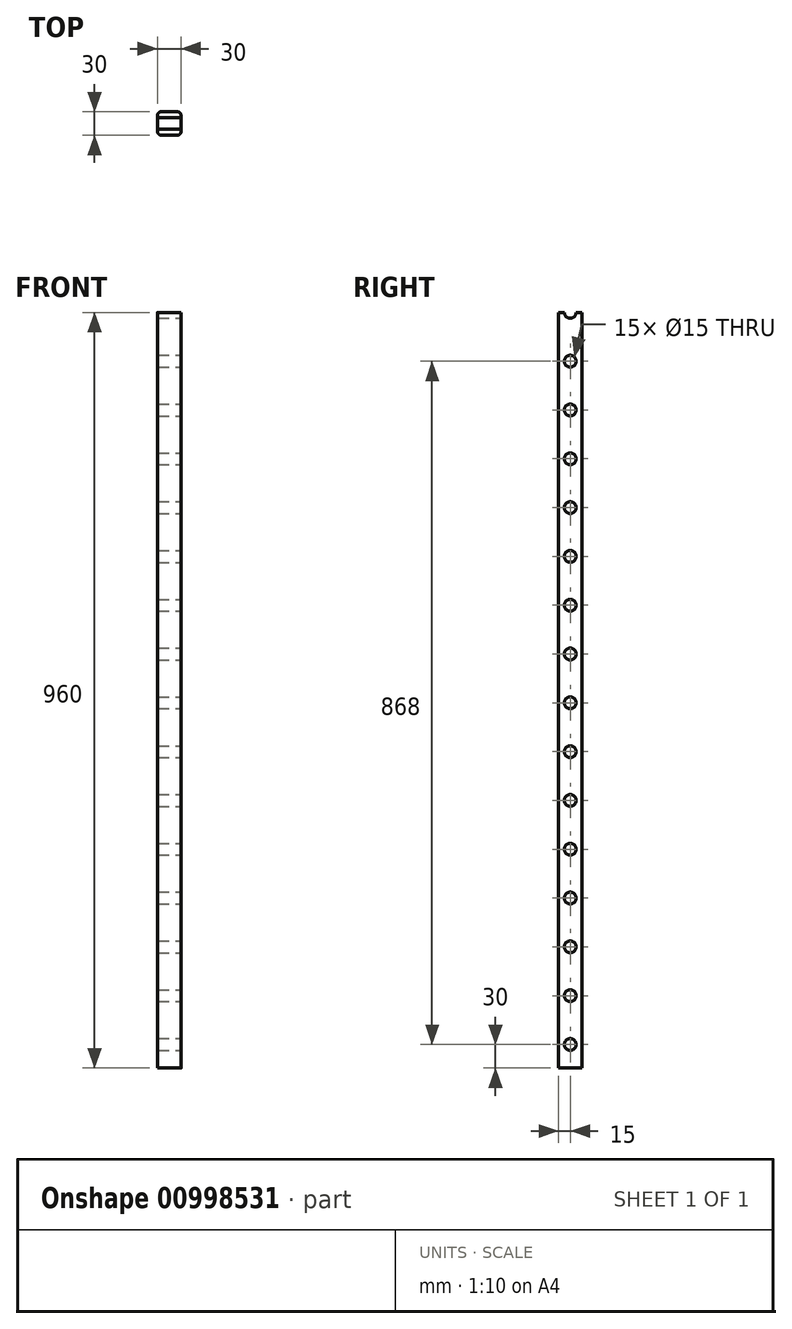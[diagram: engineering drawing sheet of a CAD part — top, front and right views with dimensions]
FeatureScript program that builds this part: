
annotation { "Feature Type Name" : "Feature", "Feature Type Description" : "" }
export const myFeature = defineFeature(function(context is Context, id is Id, definition is map)
    precondition{}
    {
        {
            var Q0;
            Q0=qCreatedBy(makeId("Top.planeOp"),FACE);
            var sketch = newSketch(context, id + "F0", { "sketchPlane" : qUnion([Q0])});
            skLineSegment(sketch, "E0.bottom", {"start": v(15, -15) * mm, "end": v(-15, -15) * mm});
            skLineSegment(sketch, "E0.top", {"start": v(15, 15) * mm, "end": v(-15, 15) * mm});
            skLineSegment(sketch, "E0.left", {"start": v(15, -15) * mm, "end": v(15, 15) * mm});
            skLineSegment(sketch, "E0.right", {"start": v(-15, -15) * mm, "end": v(-15, 15) * mm});
            skPoint(sketch, "E0.middle", {"position": v(0, 0) * mm});
            skSolve(sketch);
        }
        {
            var Q0;
            Q0=qSketchRegion(id+"F0",true);
            extrude(context, id + "F1", {"entities" : qUnion([Q0]), "depth" : 960 * mm, "offsetDistance" : 25 * mm});
        }
        {
            var Q0;
            Q0=makeQuery(id+"F1.opExtrude","SWEPT_FACE",FACE,{"disambiguationData":[OSD([sQuery(id+"F0.wireOp",EDGE,"E0.left")])]});
            var sketch = newSketch(context, id + "F2", { "sketchPlane" : qUnion([Q0])});
            skCircle(sketch, "E1", {"center": v(0, 30) * mm, "radius": 7.5 * mm});
            skCircle(sketch, "E2.0.1.0", {"center": v(0, 92) * mm, "radius": 7.5 * mm});
            skCircle(sketch, "E2.0.2.0", {"center": v(0, 154) * mm, "radius": 7.5 * mm});
            skCircle(sketch, "E2.0.3.0", {"center": v(0, 216) * mm, "radius": 7.5 * mm});
            skCircle(sketch, "E2.0.4.0", {"center": v(0, 278) * mm, "radius": 7.5 * mm});
            skCircle(sketch, "E2.0.5.0", {"center": v(0, 340) * mm, "radius": 7.5 * mm});
            skCircle(sketch, "E2.0.6.0", {"center": v(0, 402) * mm, "radius": 7.5 * mm});
            skCircle(sketch, "E2.0.7.0", {"center": v(0, 464) * mm, "radius": 7.5 * mm});
            skCircle(sketch, "E2.0.8.0", {"center": v(0, 526) * mm, "radius": 7.5 * mm});
            skCircle(sketch, "E2.0.9.0", {"center": v(0, 588) * mm, "radius": 7.5 * mm});
            skCircle(sketch, "E2.0.10.0", {"center": v(0, 650) * mm, "radius": 7.5 * mm});
            skCircle(sketch, "E2.0.11.0", {"center": v(0, 712) * mm, "radius": 7.5 * mm});
            skCircle(sketch, "E2.0.12.0", {"center": v(0, 774) * mm, "radius": 7.5 * mm});
            skCircle(sketch, "E2.0.13.0", {"center": v(0, 836) * mm, "radius": 7.5 * mm});
            skCircle(sketch, "E2.0.14.0", {"center": v(0, 898) * mm, "radius": 7.5 * mm});
            skCircle(sketch, "E2.0.15.0", {"center": v(0, 960) * mm, "radius": 7.5 * mm});
            skCircle(sketch, "E2.0.16.0", {"center": v(0, 1022) * mm, "radius": 7.5 * mm});
            skCircle(sketch, "E2.0.17.0", {"center": v(0, 1084) * mm, "radius": 7.5 * mm});
            skCircle(sketch, "E2.0.18.0", {"center": v(0, 1146) * mm, "radius": 7.5 * mm});
            skCircle(sketch, "E2.0.19.0", {"center": v(0, 1208) * mm, "radius": 7.5 * mm});
            skCircle(sketch, "E2.0.20.0", {"center": v(0, 1270) * mm, "radius": 7.5 * mm});
            skCircle(sketch, "E2.0.21.0", {"center": v(0, 1332) * mm, "radius": 7.5 * mm});
            skCircle(sketch, "E2.0.22.0", {"center": v(0, 1394) * mm, "radius": 7.5 * mm});
            skCircle(sketch, "E2.0.23.0", {"center": v(0, 1456) * mm, "radius": 7.5 * mm});
            skCircle(sketch, "E2.0.24.0", {"center": v(0, 1518) * mm, "radius": 7.5 * mm});
            skCircle(sketch, "E2.0.25.0", {"center": v(0, 1580) * mm, "radius": 7.5 * mm});
            skCircle(sketch, "E2.0.26.0", {"center": v(0, 1642) * mm, "radius": 7.5 * mm});
            skCircle(sketch, "E2.0.27.0", {"center": v(0, 1704) * mm, "radius": 7.5 * mm});
            skLineSegment(sketch, "E2.direction1", {"start": v(0, 30) * mm, "end": v(25, 30) * mm, "construction": true});
            skLineSegment(sketch, "E2.direction2", {"start": v(0, 30) * mm, "end": v(0, 92) * mm, "construction": true});
            skSolve(sketch);
        }
        {
            var Q0;
            Q0=qSketchRegion(id+"F2",true);
            extrude(context, id + "F3", {"entities" : qUnion([Q0]), "operationType" : NewBodyOperationType.REMOVE, "endBound" : BoundingType.THROUGH_ALL, "oppositeDirection" : true, "depth" : 25 * mm, "offsetDistance" : 25 * mm});
        }
        {
            var Q0;
            Q0=makeQuery(id+"F1.opExtrude","SWEPT_EDGE",EDGE,{"disambiguationData":[OSD([sQuery(id+"F0.wireOp",EDGE,"E0.bottom"),sQuery(id+"F0.wireOp",EDGE,"E0.left")])]});
            var Q1;
            Q1=makeQuery(id+"F1.opExtrude","SWEPT_EDGE",EDGE,{"disambiguationData":[OSD([sQuery(id+"F0.wireOp",EDGE,"E0.bottom"),sQuery(id+"F0.wireOp",EDGE,"E0.right")])]});
            var Q2;
            Q2=makeQuery(id+"F1.opExtrude","SWEPT_EDGE",EDGE,{"disambiguationData":[OSD([sQuery(id+"F0.wireOp",EDGE,"E0.top"),sQuery(id+"F0.wireOp",EDGE,"E0.left")])]});
            var Q3;
            Q3=makeQuery(id+"F1.opExtrude","SWEPT_EDGE",EDGE,{"disambiguationData":[OSD([sQuery(id+"F0.wireOp",EDGE,"E0.top"),sQuery(id+"F0.wireOp",EDGE,"E0.right")])]});
            fillet(context, id + "F4", {"entities" : qUnion([Q0, Q1, Q2, Q3]), "radius" : 5 * mm, "tangentPropagation" : true, "allowEdgeOverflow" : false});
        }
    });
